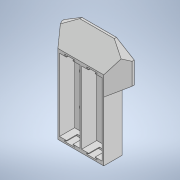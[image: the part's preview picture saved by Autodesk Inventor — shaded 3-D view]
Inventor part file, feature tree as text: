
AUTODESK INVENTOR PART (.ipt)
format: ipt  version: 2021 (Build 250183000, 183)  size: 288,256 bytes
history: native  units: mm
features: sketch x7, extrude x6, chamfer x3, projected_geometry x3
ambient origin geometry x8: Origin, YZ Plane, XZ Plane, XY Plane, X Axis, Y Axis, Z Axis, Center Point
bodies: Solid1 (feature_tree)
feature tree (19):
  extrude  "Extrusion1"  Depth=42.5mm
  sketch  "Sketch2"  dims[d2=24.0mm d3=12.0mm]
  extrude  "Extrusion2"  Depth=12.0mm
  extrude  "Extrusion3"  Depth=14.5mm
  extrude  "Extrusion4"  Depth=3.0mm TaperAngle=0.0deg
  extrude  "Extrusion5"  Depth=2.0mm TaperAngle=0.0deg
  extrude  "Extrusion6"  Depth=1.5mm
  chamfer  "Chamfer1"  Distance=14.0mm
  chamfer  "Chamfer3"  Distance=1.0mm
  chamfer  "Chamfer2"  Distance=9.5mm
  sketch  "Sketch1"  dims[d0=42.5mm d1=73.0mm]
  sketch  "Sketch3"  dims[d4=29.0mm d5=14.5mm]
  sketch  "Sketch4"  dims[d6=3.2mm d7=3.0mm d8=0.0mm]
  sketch  "Sketch5"  dims[d9=6.5mm d10=2.0mm d11=0.0mm]
  sketch  "Sketch6"  dims[d12=1.5mm d13=1.5mm]
  projected_geometry  "Projected Loop1"
  projected_geometry  "Projected Loop2"
  projected_geometry  "Projected Loop3"
  sketch  "Sketch7"  dims[d14=0.75mm d15=14.0mm d16=0.0mm d17=1.0mm d18=9.5mm d19=6.0mm d20=0.6mm d21=14.0mm d22=0.0mm d23=4.0mm d24=0.0mm d25=32.0mm d26=19.0mm d28=65.0mm d29=10.0mm d30=20.0mm d31=21.156881mm d32=2.0mm d33=0.0mm d34=15.0mm d35=11.25mm d36=45.0deg d37=15.0mm d38=19.0mm d39=45.0deg d40=11.25mm d41=15.0mm d42=45.0deg]
